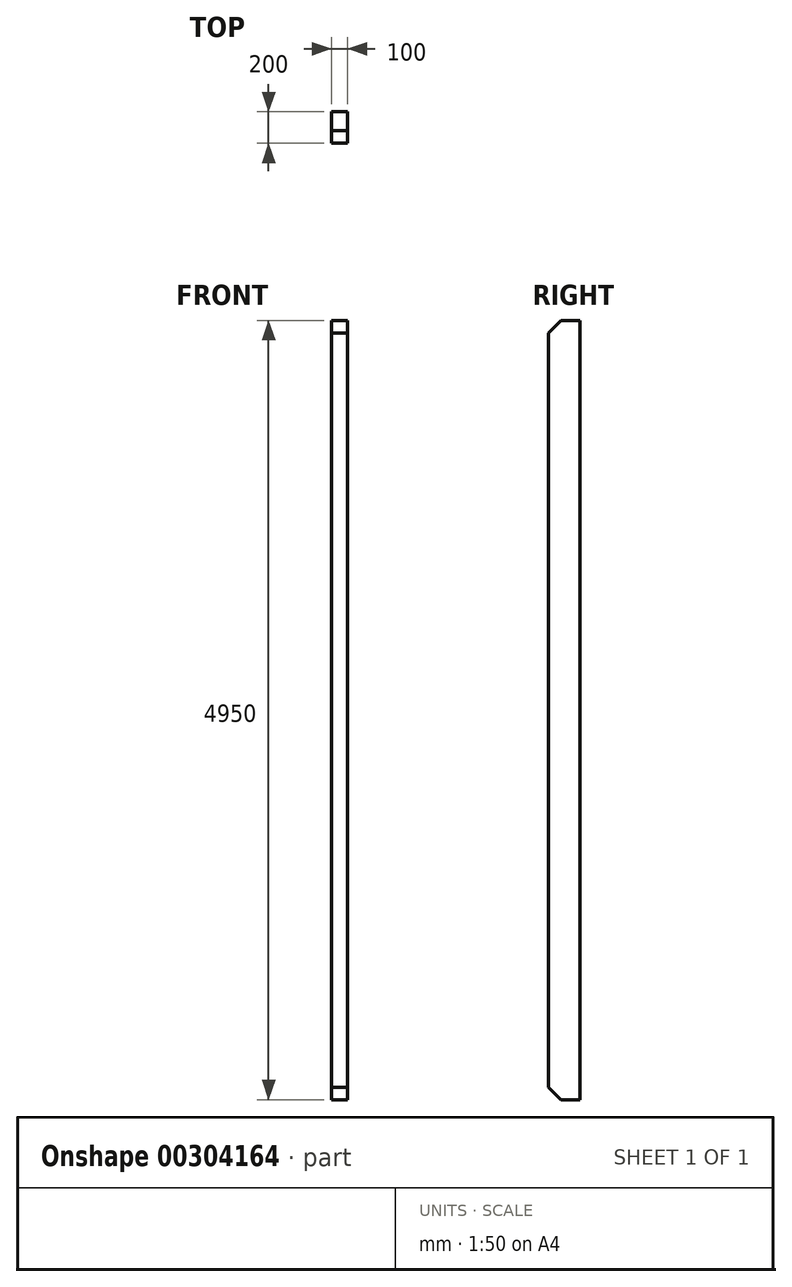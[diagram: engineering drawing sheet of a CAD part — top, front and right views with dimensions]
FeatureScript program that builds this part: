
annotation { "Feature Type Name" : "Feature", "Feature Type Description" : "" }
export const myFeature = defineFeature(function(context is Context, id is Id, definition is map)
    precondition{}
    {
        {
            var Q0;
            Q0=qCreatedBy(makeId("Top.planeOp"),FACE);
            var sketch = newSketch(context, id + "F0", { "sketchPlane" : qUnion([Q0])});
            skLineSegment(sketch, "E0.bottom", {"start": v(-60.93, 91.73) * mm, "end": v(39.07, 91.73) * mm});
            skLineSegment(sketch, "E0.top", {"start": v(-60.93, -108.27) * mm, "end": v(39.07, -108.27) * mm});
            skLineSegment(sketch, "E0.left", {"start": v(-60.93, 91.73) * mm, "end": v(-60.93, -108.27) * mm});
            skLineSegment(sketch, "E0.right", {"start": v(39.07, 91.73) * mm, "end": v(39.07, -108.27) * mm});
            skSolve(sketch);
        }
        {
            var Q0;
            Q0=makeQuery(id+"F0.imprint","IMPRINT",FACE,{"disambiguationData":[TD([[makeQuery(id+"F0.imprint","IMPRINT",EDGE,{"derivedFrom":sQuery(id+"F0.wireOp",EDGE,"E0.bottom")}),-1.0]])]});
            extrude(context, id + "F1", {"entities" : qUnion([Q0]), "depth" : 4950 * mm});
        }
        {
            var Q0;
            Q0=makeQuery(id+"F1.opExtrude","CAP_EDGE",EDGE,{"disambiguationData":[OSD([sQuery(id+"F0.wireOp",EDGE,"E0.top")])],"isStart":false});
            chamfer(context, id + "F2", {"entities" : qUnion([Q0]), "width" : 80 * mm, "tangentPropagation" : true});
        }
        {
            var Q0;
            Q0=makeQuery(id+"F1.opExtrude","CAP_EDGE",EDGE,{"disambiguationData":[OSD([sQuery(id+"F0.wireOp",EDGE,"E0.top")])],"isStart":true});
            chamfer(context, id + "F3", {"entities" : qUnion([Q0]), "width" : 80 * mm, "tangentPropagation" : true});
        }
    });
